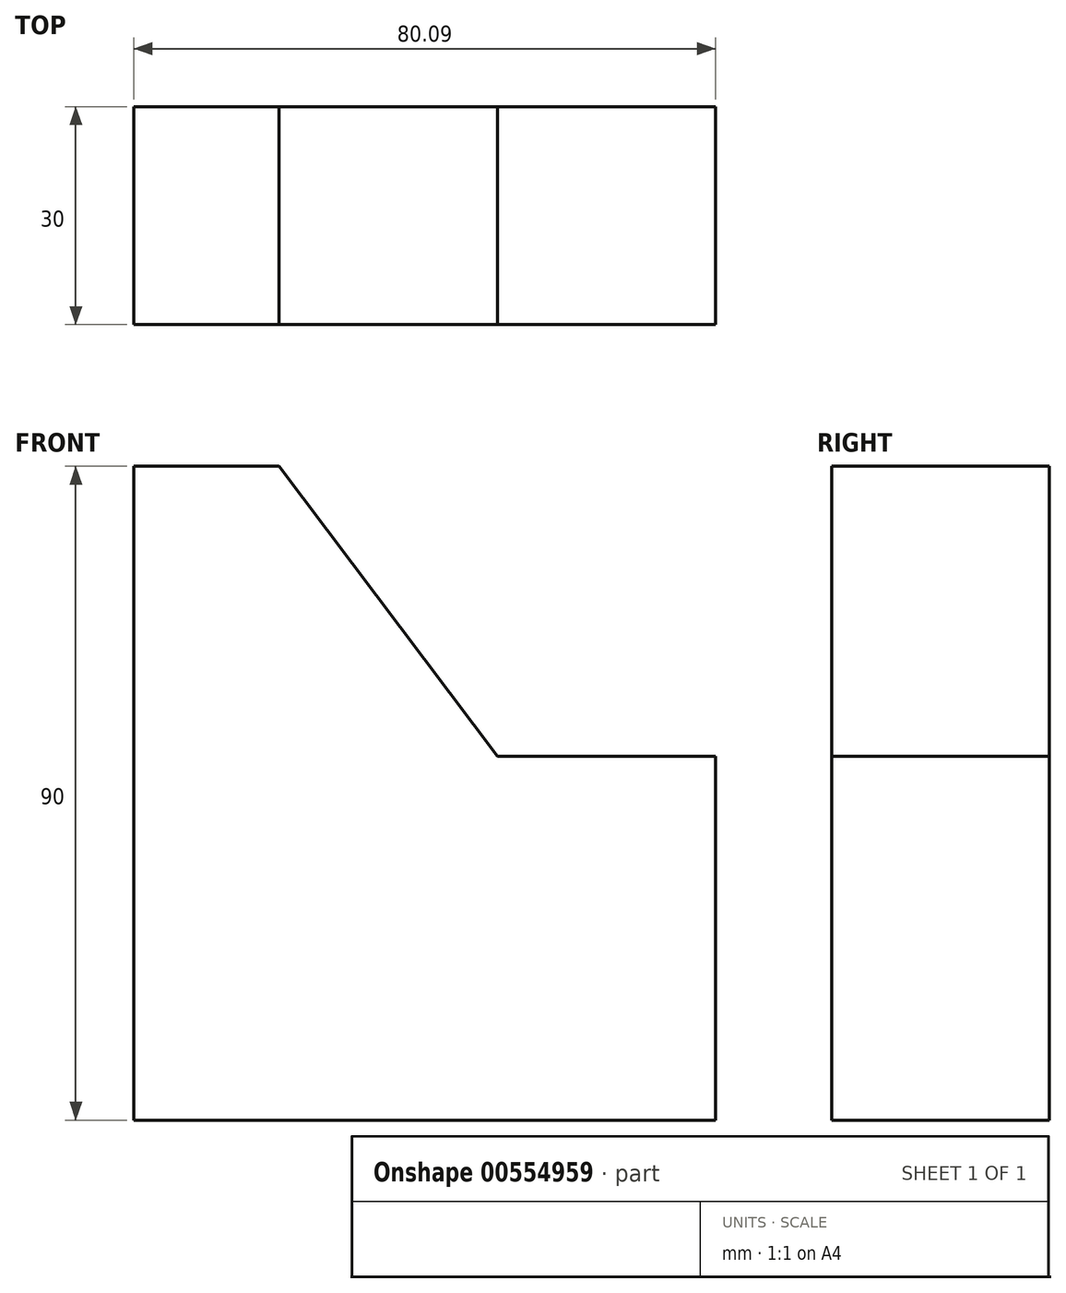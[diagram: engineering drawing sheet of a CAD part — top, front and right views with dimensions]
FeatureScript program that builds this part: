
annotation { "Feature Type Name" : "Feature", "Feature Type Description" : "" }
export const myFeature = defineFeature(function(context is Context, id is Id, definition is map)
    precondition{}
    {
        {
            var Q0;
            Q0=qCreatedBy(makeId("Front.planeOp"),FACE);
            var sketch = newSketch(context, id + "F0", { "sketchPlane" : qUnion([Q0])});
            skLineSegment(sketch, "E0", {"start": v(-56.44, 33.34) * mm, "end": v(-56.44, -56.66) * mm});
            skLineSegment(sketch, "E1", {"start": v(-56.44, -56.66) * mm, "end": v(23.65, -56.66) * mm});
            skLineSegment(sketch, "E2", {"start": v(23.65, -56.66) * mm, "end": v(23.65, -6.59) * mm});
            skLineSegment(sketch, "E3", {"start": v(23.65, -6.59) * mm, "end": v(-6.35, -6.59) * mm});
            skLineSegment(sketch, "E4", {"start": v(-56.44, 33.34) * mm, "end": v(-36.44, 33.34) * mm});
            skLineSegment(sketch, "E5", {"start": v(-36.44, 33.34) * mm, "end": v(-6.35, -6.59) * mm});
            skLineSegment(sketch, "E6", {"start": v(-36.44, 33.34) * mm, "end": v(-36.44, 2.88) * mm});
            skLineSegment(sketch, "E7", {"start": v(-6.35, -6.59) * mm, "end": v(-22.93, -6.59) * mm});
            skSolve(sketch);
        }
        {
            var Q0;
            Q0 = qSketchRegion(id + "F0", true);
            extrude(context, id + "F1", {"entities" : qUnion([Q0]), "depth" : 30 * mm, "offsetDistance" : 25 * mm});
        }
    });
